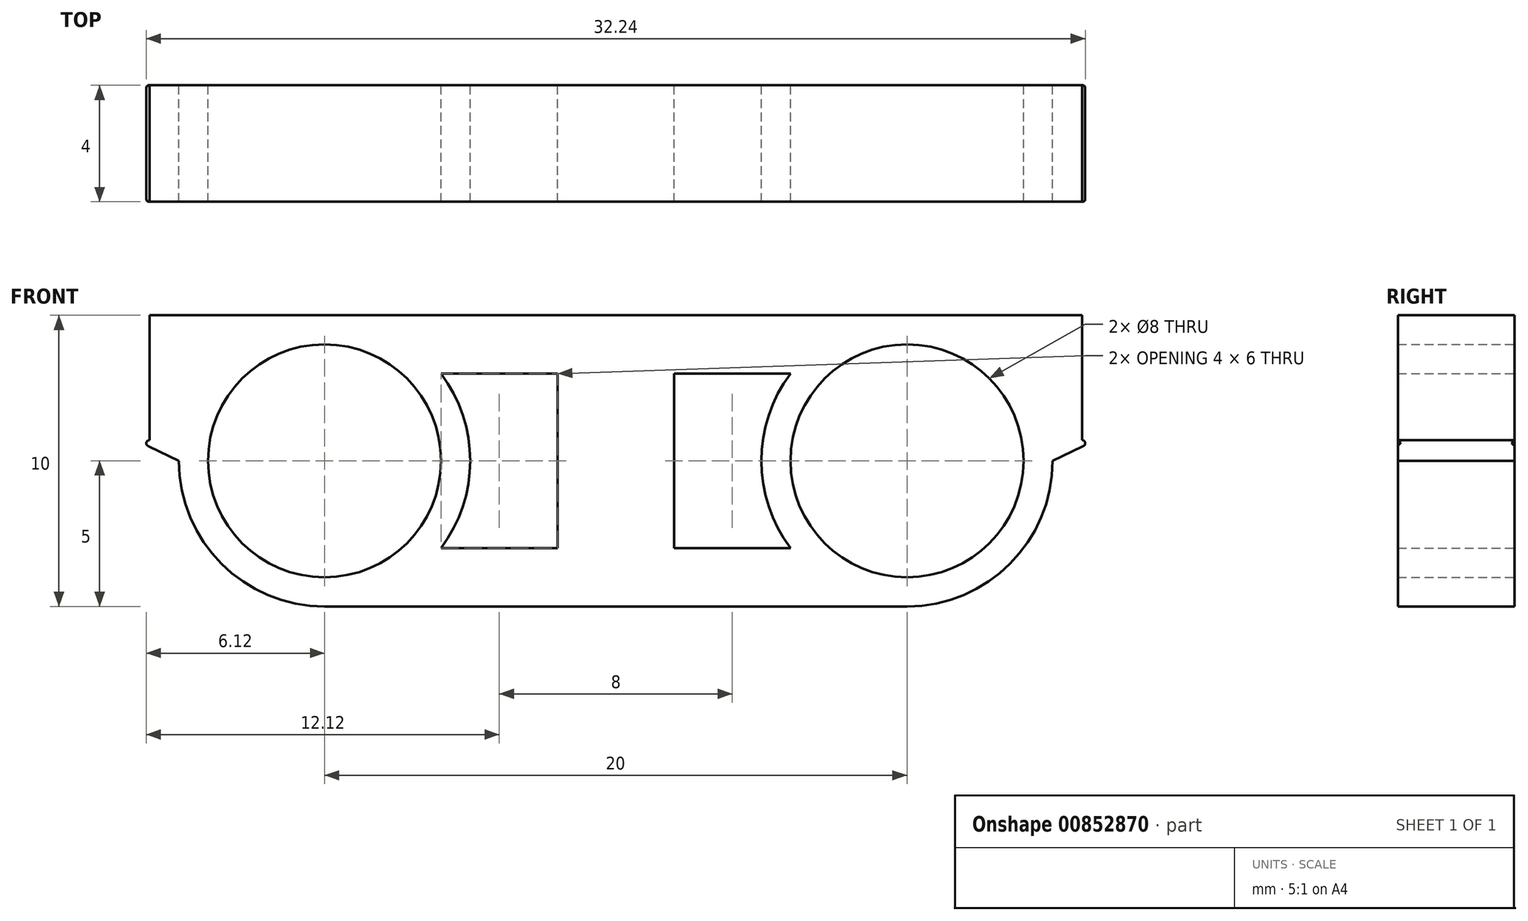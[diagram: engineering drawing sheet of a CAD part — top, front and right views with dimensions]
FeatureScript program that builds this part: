
annotation { "Feature Type Name" : "Feature", "Feature Type Description" : "" }
export const myFeature = defineFeature(function(context is Context, id is Id, definition is map)
    precondition{}
    {
        {
            var Q0;
            Q0=qCreatedBy(makeId("Front.planeOp"),FACE);
            var sketch = newSketch(context, id + "F0", { "sketchPlane" : qUnion([Q0])});
            skCircle(sketch, "E0", {"center": v(0, 0) * mm, "radius": 4 * mm});
            skCircle(sketch, "E1", {"center": v(0, 0) * mm, "radius": 5 * mm});
            skSolve(sketch);
        }
        {
            var Q0;
            Q0 = qSketchRegion(id + "F0", true);
            extrude(context, id + "F1", {"entities" : qUnion([Q0]), "depth" : 4 * mm, "offsetDistance" : 25 * mm});
        }
        {
            var Q0;
            Q0=qCreatedBy(makeId("Front.planeOp"),FACE);
            var sketch = newSketch(context, id + "F2", { "sketchPlane" : qUnion([Q0])});
            skLineSegment(sketch, "E2", {"start": v(0, 0) * mm, "end": v(-7.62, 0.77) * mm, "construction": true});
            skCircle(sketch, "E3.0", {"center": v(0, 0) * mm, "radius": 5 * mm, "construction": true});
            skLineSegment(sketch, "E4", {"start": v(-6.32, 0.63) * mm, "end": v(-4.9, 1) * mm});
            skLineSegment(sketch, "E5.MirrorCS", {"start": v(-6.32, 0.63) * mm, "end": v(-5, 0) * mm});
            skLineSegment(sketch, "E6", {"start": v(-4.9, 1) * mm, "end": v(-5, 0) * mm});
            skLineSegment(sketch, "E7", {"start": v(-6.11, 0.69) * mm, "end": v(-6.13, 0.54) * mm});
            skSolve(sketch);
        }
        {
            var Q0;
            {var subQ0=sQuery(id+"F2.wireOp",EDGE,"E6");Q0=makeQuery(id+"F2.imprint","IMPRINT",FACE,{"disambiguationData":[TD([[makeQuery(id+"F2.imprint","IMPRINT",EDGE,{"derivedFrom":subQ0}),-1.0]])]});}
            var Q1;
            Q1=makeQuery(id+"F1.opExtrude","CAP_FACE",FACE,{"disambiguationData":[OSD([sQuery(id+"F0.wireOp",EDGE,"E0"),sQuery(id+"F0.wireOp",EDGE,"E1")])],"isStart":false});
            extrude(context, id + "F3", {"entities" : qUnion([Q0]), "operationType" : NewBodyOperationType.ADD, "endBound" : BoundingType.UP_TO_SURFACE, "depth" : 25 * mm, "endBoundEntityFace" : qUnion([Q1]), "offsetDistance" : 25 * mm});
        }
        {
            var Q0;
            Q0=makeQuery(id+"F3.opExtrude","SWEPT_FACE",FACE,{"disambiguationData":[OSD([sQuery(id+"F2.wireOp",EDGE,"E7")])]});
            fillet(context, id + "F4", {"entities" : qUnion([Q0]), "radius" : .1 * mm, "allowEdgeOverflow" : false});
        }
        {
            var Q0;
            Q0=qCreatedBy(makeId("Front.planeOp"),FACE);
            var sketch = newSketch(context, id + "F5", { "sketchPlane" : qUnion([Q0])});
            skArc(sketch, "E8.0", {"start": v(-0.7, -4.95) * mm, "mid": v(4.99, -0.35) * mm, "end": v(0, 5) * mm});
            skLineSegment(sketch, "E9", {"start": v(0, 5) * mm, "end": v(10, 5) * mm});
            skLineSegment(sketch, "E10", {"start": v(0, -5) * mm, "end": v(10, -5) * mm});
            skLineSegment(sketch, "E11", {"start": v(10, 5) * mm, "end": v(10, -5) * mm});
            skPoint(sketch, "E12.orphan", {"position": v(-4.9, 1) * mm});
            skLineSegment(sketch, "E13.0", {"start": v(4, -3) * mm, "end": v(8, -3) * mm});
            skLineSegment(sketch, "E13.1", {"start": v(8, 3) * mm, "end": v(8, -3) * mm});
            skLineSegment(sketch, "E13.2", {"start": v(4, 3) * mm, "end": v(8, 3) * mm});
            skSolve(sketch);
        }
        {
            var Q0;
            {var subQ1=sQuery(id+"F5.wireOp",EDGE,"E9");Q0=makeQuery(id+"F5.imprint","IMPRINT",FACE,{"disambiguationData":[TD([[makeQuery(id+"F5.imprint","IMPRINT",EDGE,{"derivedFrom":subQ1}),-1.0]])]});}
            var Q1;
            {var subQ0=sQuery(id+"F0.wireOp",EDGE,"E1");var subQ1=sQuery(id+"F0.wireOp",EDGE,"E0");Q1=makeQuery(id+"FleiXFo7CVz2GXt_1.7.F3.boolean.opBoolean","MERGE",FACE,{"derivedFrom":[makeQuery(id+"FleiXFo7CVz2GXt_1.6.F3.boolean.opBoolean","MERGE",FACE,{"derivedFrom":[makeQuery(id+"FleiXFo7CVz2GXt_1.5.F3.boolean.opBoolean","MERGE",FACE,{"derivedFrom":[makeQuery(id+"FleiXFo7CVz2GXt_1.4.F3.boolean.opBoolean","MERGE",FACE,{"derivedFrom":[makeQuery(id+"FleiXFo7CVz2GXt_1.3.F3.boolean.opBoolean","MERGE",FACE,{"derivedFrom":[makeQuery(id+"FleiXFo7CVz2GXt_1.2.F3.boolean.opBoolean","MERGE",FACE,{"derivedFrom":[makeQuery(id+"FleiXFo7CVz2GXt_1.1.F3.boolean.opBoolean","MERGE",FACE,{"derivedFrom":[makeQuery(id+"F3.boolean.opBoolean","MERGE",FACE,{"derivedFrom":[makeQuery(id+"F1.opExtrude","CAP_FACE",FACE,{"disambiguationData":[OSD([subQ1,subQ0])],"isStart":false}),makeQuery(id+"F3.opExtrude","CAP_FACE",FACE,{"disambiguationData":[OSD([subQ1,subQ0])],"isStart":false})]}),makeQuery(id+"FleiXFo7CVz2GXt_1.1.F3.opExtrude","CAP_FACE",FACE,{"disambiguationData":[OSD([subQ1,subQ0])],"isStart":false})]}),makeQuery(id+"FleiXFo7CVz2GXt_1.2.F3.opExtrude","CAP_FACE",FACE,{"disambiguationData":[OSD([subQ1,subQ0])],"isStart":false})]}),makeQuery(id+"FleiXFo7CVz2GXt_1.3.F3.opExtrude","CAP_FACE",FACE,{"disambiguationData":[OSD([subQ1,subQ0])],"isStart":false})]}),makeQuery(id+"FleiXFo7CVz2GXt_1.4.F3.opExtrude","CAP_FACE",FACE,{"disambiguationData":[OSD([subQ1,subQ0])],"isStart":false})]}),makeQuery(id+"FleiXFo7CVz2GXt_1.5.F3.opExtrude","CAP_FACE",FACE,{"disambiguationData":[OSD([subQ1,subQ0])],"isStart":false})]}),makeQuery(id+"FleiXFo7CVz2GXt_1.6.F3.opExtrude","CAP_FACE",FACE,{"disambiguationData":[OSD([subQ1,subQ0])],"isStart":false})]}),makeQuery(id+"FleiXFo7CVz2GXt_1.7.F3.opExtrude","CAP_FACE",FACE,{"disambiguationData":[OSD([subQ1,subQ0])],"isStart":false})]});}
            extrude(context, id + "F6", {"entities" : qUnion([Q0]), "operationType" : NewBodyOperationType.ADD, "endBound" : BoundingType.UP_TO_SURFACE, "depth" : 25 * mm, "endBoundEntityFace" : qUnion([Q1]), "offsetDistance" : 25 * mm});
        }
        {
            var Q0;
            Q0=makeQuery(id+"F1.opExtrude","SWEPT_BODY",BODY,{"disambiguationData":[OSD([sQuery(id+"F0.wireOp",EDGE,"E0"),sQuery(id+"F0.wireOp",EDGE,"E1")])]});
            var Q1;
            Q1=makeQuery(id+"F6.opExtrude","SWEPT_FACE",FACE,{"disambiguationData":[OSD([sQuery(id+"F5.wireOp",EDGE,"E11")])]});
            mirror(context, id + "F7", {"operationType" : NewBodyOperationType.ADD, "entities" : qUnion([Q0]), "mirrorPlane" : qUnion([Q1])});
        }
        {
            var Q0;
            Q0=qCreatedBy(makeId("Front.planeOp"),FACE);
            var sketch = newSketch(context, id + "F8", { "sketchPlane" : qUnion([Q0])});
            skArc(sketch, "E14.0", {"start": v(0, 5) * mm, "mid": v(-3.16, 3.87) * mm, "end": v(-4.9, 1) * mm});
            skArc(sketch, "E15.0", {"start": v(20, 5) * mm, "mid": v(23.16, 3.87) * mm, "end": v(24.9, 1) * mm});
            skLineSegment(sketch, "E16.0", {"start": v(-6, 0.71) * mm, "end": v(-4.9, 1) * mm});
            skLineSegment(sketch, "E17.0", {"start": v(26, 0.71) * mm, "end": v(24.9, 1) * mm});
            skLineSegment(sketch, "E18", {"start": v(-6, 0.71) * mm, "end": v(-6, 5) * mm});
            skLineSegment(sketch, "E19", {"start": v(-6, 5) * mm, "end": v(0, 5) * mm});
            skLineSegment(sketch, "E20", {"start": v(26, 0.71) * mm, "end": v(26, 5) * mm});
            skLineSegment(sketch, "E21", {"start": v(26, 5) * mm, "end": v(20, 5) * mm});
            skSolve(sketch);
        }
        {
            var Q0;
            Q0 = qSketchRegion(id + "F8", true);
            var Q1;
            {var subQ0=sQuery(id+"F0.wireOp",EDGE,"E1");var subQ1=sQuery(id+"F0.wireOp",EDGE,"E0");var subQ2=makeQuery(id+"F6.boolean.opBoolean","MERGE",FACE,{"derivedFrom":[makeQuery(id+"FleiXFo7CVz2GXt_1.7.F3.boolean.opBoolean","MERGE",FACE,{"derivedFrom":[makeQuery(id+"FleiXFo7CVz2GXt_1.6.F3.boolean.opBoolean","MERGE",FACE,{"derivedFrom":[makeQuery(id+"FleiXFo7CVz2GXt_1.5.F3.boolean.opBoolean","MERGE",FACE,{"derivedFrom":[makeQuery(id+"FleiXFo7CVz2GXt_1.4.F3.boolean.opBoolean","MERGE",FACE,{"derivedFrom":[makeQuery(id+"FleiXFo7CVz2GXt_1.3.F3.boolean.opBoolean","MERGE",FACE,{"derivedFrom":[makeQuery(id+"FleiXFo7CVz2GXt_1.2.F3.boolean.opBoolean","MERGE",FACE,{"derivedFrom":[makeQuery(id+"FleiXFo7CVz2GXt_1.1.F3.boolean.opBoolean","MERGE",FACE,{"derivedFrom":[makeQuery(id+"F3.boolean.opBoolean","MERGE",FACE,{"derivedFrom":[makeQuery(id+"F1.opExtrude","CAP_FACE",FACE,{"disambiguationData":[OSD([subQ1,subQ0])],"isStart":false}),makeQuery(id+"F3.opExtrude","CAP_FACE",FACE,{"disambiguationData":[OSD([subQ1,subQ0])],"isStart":false})]}),makeQuery(id+"FleiXFo7CVz2GXt_1.1.F3.opExtrude","CAP_FACE",FACE,{"disambiguationData":[OSD([subQ1,subQ0])],"isStart":false})]}),makeQuery(id+"FleiXFo7CVz2GXt_1.2.F3.opExtrude","CAP_FACE",FACE,{"disambiguationData":[OSD([subQ1,subQ0])],"isStart":false})]}),makeQuery(id+"FleiXFo7CVz2GXt_1.3.F3.opExtrude","CAP_FACE",FACE,{"disambiguationData":[OSD([subQ1,subQ0])],"isStart":false})]}),makeQuery(id+"FleiXFo7CVz2GXt_1.4.F3.opExtrude","CAP_FACE",FACE,{"disambiguationData":[OSD([subQ1,subQ0])],"isStart":false})]}),makeQuery(id+"FleiXFo7CVz2GXt_1.5.F3.opExtrude","CAP_FACE",FACE,{"disambiguationData":[OSD([subQ1,subQ0])],"isStart":false})]}),makeQuery(id+"FleiXFo7CVz2GXt_1.6.F3.opExtrude","CAP_FACE",FACE,{"disambiguationData":[OSD([subQ1,subQ0])],"isStart":false})]}),makeQuery(id+"FleiXFo7CVz2GXt_1.7.F3.opExtrude","CAP_FACE",FACE,{"disambiguationData":[OSD([subQ1,subQ0])],"isStart":false})]}),makeQuery(id+"F6.opExtrude","CAP_FACE",FACE,{"disambiguationData":[OSD([subQ1,subQ0])],"isStart":false})]});Q1=makeQuery(id+"F7.boolean.opBoolean","MERGE",FACE,{"derivedFrom":[subQ2,makeQuery(id+"F7.opPattern","COPY",FACE,{"derivedFrom":subQ2,"instanceName":"1"})]});}
            extrude(context, id + "F9", {"entities" : qUnion([Q0]), "operationType" : NewBodyOperationType.ADD, "endBound" : BoundingType.UP_TO_SURFACE, "depth" : 25 * mm, "endBoundEntityFace" : qUnion([Q1]), "offsetDistance" : 25 * mm});
        }
    });
